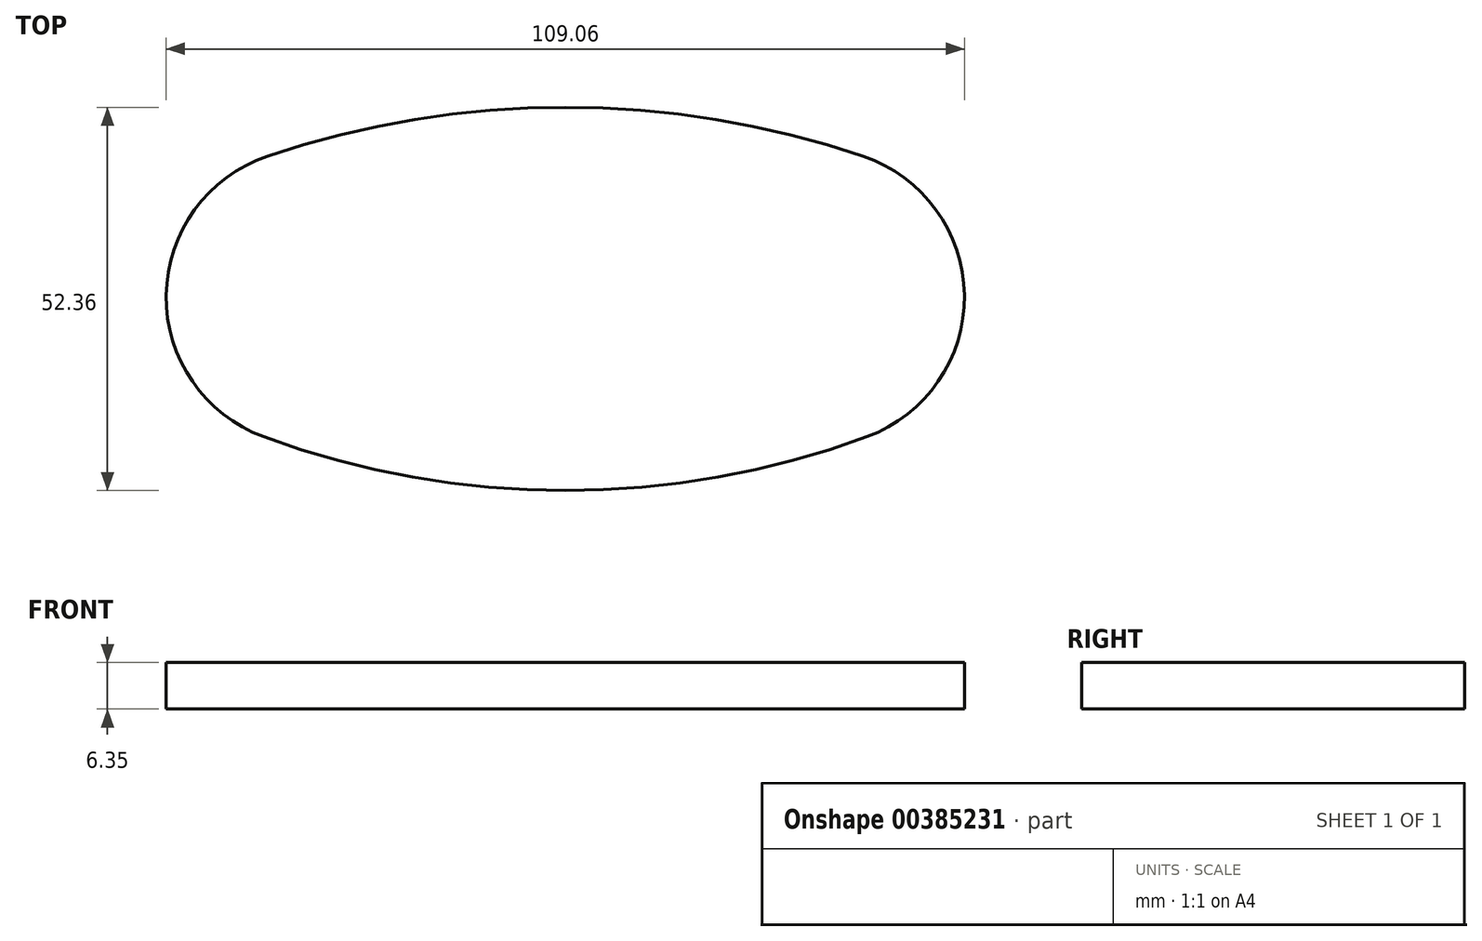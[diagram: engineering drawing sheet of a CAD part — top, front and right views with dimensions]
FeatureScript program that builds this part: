
annotation { "Feature Type Name" : "Feature", "Feature Type Description" : "" }
export const myFeature = defineFeature(function(context is Context, id is Id, definition is map)
    precondition{}
    {
        {
            var Q0;
            Q0=qCreatedBy(makeId("Top.planeOp"),FACE);
            var sketch = newSketch(context, id + "F0", { "sketchPlane" : qUnion([Q0])});
            skArc(sketch, "E0", {"start": v(75.29, 0) * mm, "mid": v(-0.6, 25.12) * mm, "end": v(-76.5, 0) * mm});
            skArc(sketch, "E1", {"start": v(-76.5, 0) * mm, "mid": v(-0.6, -27.24) * mm, "end": v(75.29, 0) * mm});
            skSolve(sketch);
        }
        {
            var Q0;
            Q0=makeQuery(id+"F0.imprint","IMPRINT",FACE,{"disambiguationData":[TD([[makeQuery(id+"F0.imprint","IMPRINT",EDGE,{"derivedFrom":sQuery(id+"F0.wireOp",EDGE,"E0")}),1.0]])]});
            extrude(context, id + "F1", {"entities" : qUnion([Q0]), "depth" : 6.35 * mm});
        }
        {
            var Q0;
            {var subQ0=sQuery(id+"F0.wireOp",EDGE,"E1");var subQ1=sQuery(id+"F0.wireOp",EDGE,"E0");Q0=makeQuery(id+"F1.opExtrude","SWEPT_EDGE",EDGE,{"disambiguationData":[OSD([subQ1,subQ0]),TDD([makeQuery(id+"F0.imprint","INTERSECT",VERTEX,{"disambiguationData":[OD(0.0)],"derivedFrom":[subQ1,subQ0]})])]});}
            var Q1;
            {var subQ0=sQuery(id+"F0.wireOp",EDGE,"E1");var subQ1=sQuery(id+"F0.wireOp",EDGE,"E0");Q1=makeQuery(id+"F1.opExtrude","SWEPT_EDGE",EDGE,{"disambiguationData":[OSD([subQ1,subQ0]),TDD([makeQuery(id+"F0.imprint","INTERSECT",VERTEX,{"disambiguationData":[OD(1.0)],"derivedFrom":[subQ1,subQ0]})])]});}
            fillet(context, id + "F2", {"entities" : qUnion([Q0, Q1]), "radius" : 20.32 * mm, "tangentPropagation" : true, "allowEdgeOverflow" : false});
        }
    });
